# Revit family: SC Duplex 12 fibres
name_source: partatom
category: Installations électriques
units: mm (PartAtom-declared; Revit-internal decimal feet)

## family parameters
Basée sur le plan de construction = Non
Conserver l'orientation des annotations = Non
Cote de connecteur circulaire = Utiliser le diamètre
Couper avec des vides une fois chargée = Non
Partagée = Non
Point de calcul de pièce = Non
Toujours verticalement = Oui
Type d'élément = Normal

## types (2) — shared parameters
Classe ETIM = EC001130
Couleur = IDS_NOIR
Fonction = Panneaux de brassage à connecteur optique Legrand
Hauteur = 23 mm  [stored 0.0754593 ft]
Hauteur de l'ouverture = 1 mm  [stored 0.00328084 ft]
Hauteur des connecteurs = 10 mm  [stored 0.0328084 ft]
IK = IK04
IP = IP20
Largeur (mm) = 108.8 mm  [stored 0.356955 ft]
Largeur de l'ouverture = 6 mm  [stored 0.019685 ft]
Largeur des connecteurs = 26 mm  [stored 0.0853018 ft]
Lien e-catalogue = https://www.legrand.fr
Nombre de connecteurs = 12
Profondeur = 33.3 mm  [stored 0.109252 ft]
RAL = 9017
Température de fonctionnement = -10°C à 60°C
Température de stockage = -10°C à 60°C
Type de connecteur externe = SC_DUPLEX
Type de connecteur interne = SC_DUPLEX
zero-valued in all types: Elévation par défaut

## per-type parameters (varying)
| type | Couleur des connecteurs | EAN | Référence Legrand | Type de fibre optique |
| Bloc SC Duplex HD 12 fibres multimode | IDS_JAUNE | 3414970961839 | 032121 | Multimode |
| Bloc SC Duplex HD 12 fibres monomode | IDS_BLEU | 3414970961679 | 032111 | Monomode |

note: column(s) folded — value = type name in every type: Libellé BIM

note: [stored X ft] marks values corroborated as IEEE doubles in the binary element streams (Revit-internal decimal feet)
